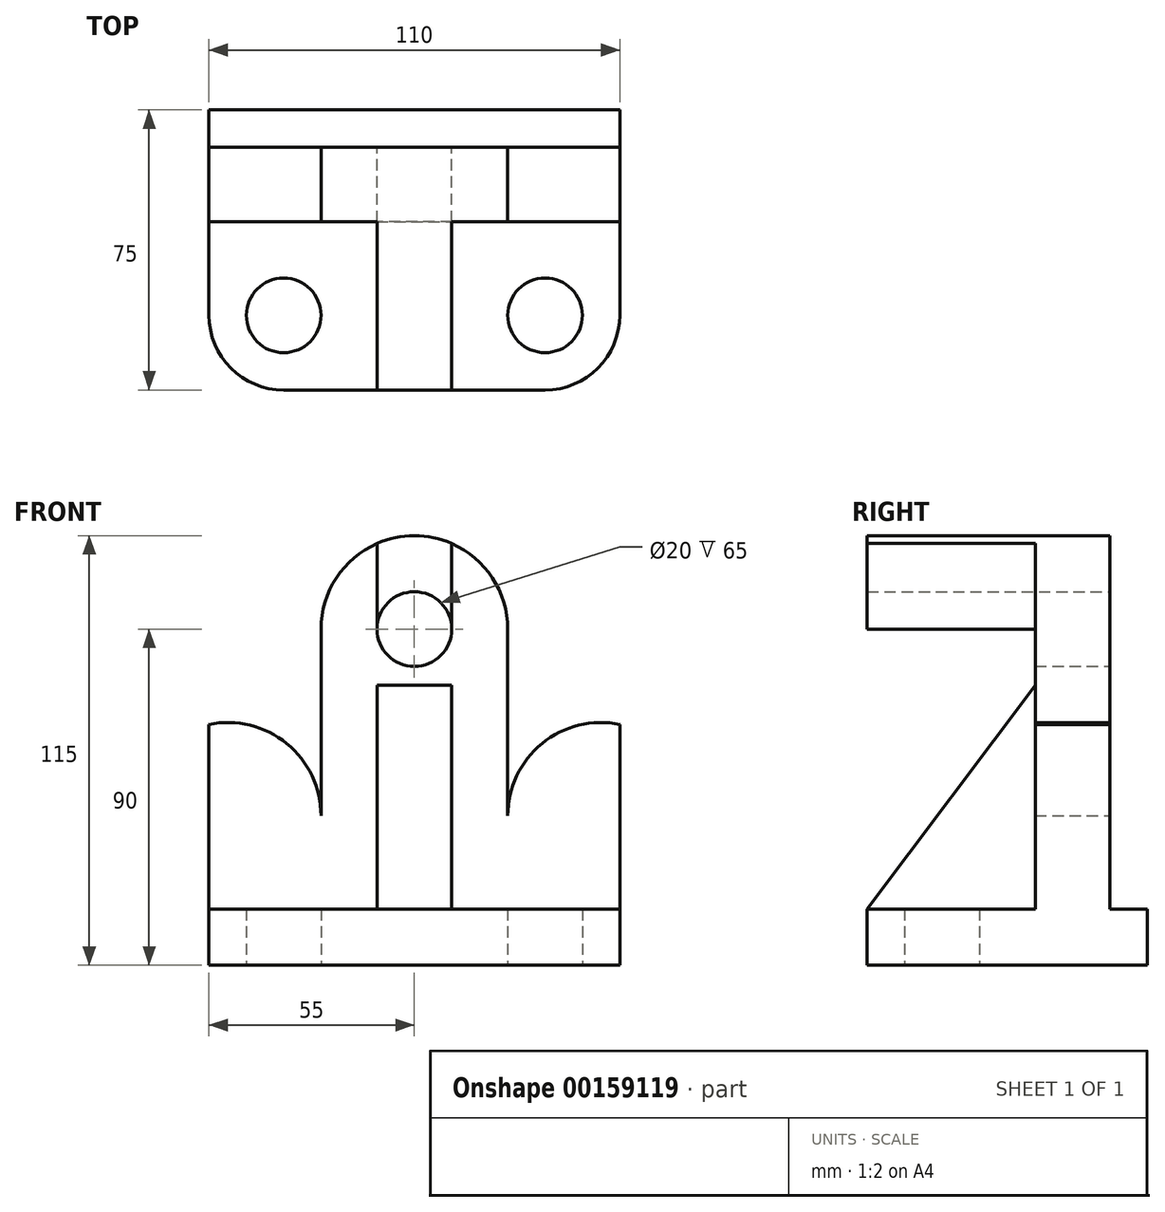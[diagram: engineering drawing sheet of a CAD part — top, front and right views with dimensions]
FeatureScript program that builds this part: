
annotation { "Feature Type Name" : "Feature", "Feature Type Description" : "" }
export const myFeature = defineFeature(function(context is Context, id is Id, definition is map)
    precondition{}
    {
        {
            var Q0;
            Q0=qCreatedBy(makeId("Top.planeOp"),FACE);
            var sketch = newSketch(context, id + "F0", { "sketchPlane" : qUnion([Q0])});
            skLineSegment(sketch, "E0.bottom", {"start": v(0, 0) * mm, "end": v(110, 0) * mm});
            skLineSegment(sketch, "E0.top", {"start": v(0, -75) * mm, "end": v(110, -75) * mm});
            skLineSegment(sketch, "E0.left", {"start": v(0, 0) * mm, "end": v(0, -75) * mm});
            skLineSegment(sketch, "E0.right", {"start": v(110, 0) * mm, "end": v(110, -75) * mm});
            skSolve(sketch);
        }
        {
            var Q0;
            Q0 = qSketchRegion(id + "F0", true);
            extrude(context, id + "F1", {"entities" : qUnion([Q0]), "depth" : (23 * 5) * mm});
        }
        {
            var Q0;
            Q0=makeQuery(id+"F1.opExtrude","SWEPT_FACE",FACE,{"disambiguationData":[OSD([sQuery(id+"F0.wireOp",EDGE,"E0.right")])]});
            var sketch = newSketch(context, id + "F2", { "sketchPlane" : qUnion([Q0])});
            skLineSegment(sketch, "E1.bottom", {"start": v(0, 115) * mm, "end": v(-10, 115) * mm});
            skLineSegment(sketch, "E1.top", {"start": v(0, 15) * mm, "end": v(-10, 15) * mm});
            skLineSegment(sketch, "E1.left", {"start": v(0, 115) * mm, "end": v(0, 15) * mm});
            skLineSegment(sketch, "E1.right", {"start": v(-10, 115) * mm, "end": v(-10, 15) * mm});
            skSolve(sketch);
        }
        {
            var Q0;
            Q0 = qSketchRegion(id + "F2", true);
            extrude(context, id + "F3", {"entities" : qUnion([Q0]), "operationType" : NewBodyOperationType.REMOVE, "endBound" : BoundingType.THROUGH_ALL, "oppositeDirection" : true, "depth" : 25 * mm});
        }
        {
            var Q0;
            Q0=makeQuery(id+"F3.boolean.opBoolean","COPY",FACE,{"derivedFrom":makeQuery(id+"F3.opExtrude","SWEPT_FACE",FACE,{"disambiguationData":[OSD([sQuery(id+"F2.wireOp",EDGE,"E1.right")])]})});
            var sketch = newSketch(context, id + "F4", { "sketchPlane" : qUnion([Q0])});
            skLineSegment(sketch, "E2.bottom", {"start": v(-80, 15) * mm, "end": v(-30, 15) * mm});
            skLineSegment(sketch, "E2.top", {"start": v(-80, 115) * mm, "end": v(-30, 115) * mm});
            skLineSegment(sketch, "E2.left", {"start": v(-80, 15) * mm, "end": v(-80, 115) * mm});
            skLineSegment(sketch, "E2.right", {"start": v(-30, 15) * mm, "end": v(-30, 115) * mm});
            skCircle(sketch, "E3", {"center": v(-5, 40) * mm, "radius": 25 * mm});
            skCircle(sketch, "E4", {"center": v(-105, 40) * mm, "radius": 25 * mm});
            skCircle(sketch, "E5", {"center": v(-55, 90) * mm, "radius": 25 * mm});
            skLineSegment(sketch, "E6.bottom", {"start": v(-110, 15) * mm, "end": v(0, 15) * mm});
            skLineSegment(sketch, "E6.top", {"start": v(-110, 115) * mm, "end": v(0, 115) * mm});
            skLineSegment(sketch, "E6.left", {"start": v(-110, 15) * mm, "end": v(-110, 115) * mm});
            skLineSegment(sketch, "E6.right", {"start": v(0, 15) * mm, "end": v(0, 115) * mm});
            skCircle(sketch, "E7", {"center": v(-55, 90) * mm, "radius": 10 * mm});
            skSolve(sketch);
        }
        {
            var Q0;
            {var subQ1=sQuery(id+"F4.wireOp",EDGE,"E4");var subQ3=sQuery(id+"F4.wireOp",EDGE,"E2.left");var subQ4=makeQuery(id+"F4.imprint","INTERSECT",VERTEX,{"derivedFrom":[subQ3,subQ1]});Q0=makeQuery(id+"F4.imprint","IMPRINT",FACE,{"disambiguationData":[TD([[makeQuery(id+"F4.imprint","IMPRINT",EDGE,{"disambiguationData":[TD([[subQ4,-1.0]])],"derivedFrom":subQ3}),1.0]])]});}
            var Q1;
            {var subQ0=sQuery(id+"F4.wireOp",EDGE,"E6.left");var subQ1=sQuery(id+"F4.wireOp",EDGE,"E4");var subQ2=makeQuery(id+"F4.imprint","INTERSECT",VERTEX,{"disambiguationData":[OD(0.0)],"derivedFrom":[subQ1,subQ0]});Q1=makeQuery(id+"F4.imprint","IMPRINT",FACE,{"disambiguationData":[TD([[makeQuery(id+"F4.imprint","IMPRINT",EDGE,{"disambiguationData":[TD([[subQ2,1.0]])],"derivedFrom":subQ1}),1.0]])]});}
            var Q2;
            {var subQ0=sQuery(id+"F4.wireOp",EDGE,"E6.right");var subQ1=sQuery(id+"F4.wireOp",EDGE,"E3");var subQ2=makeQuery(id+"F4.imprint","INTERSECT",VERTEX,{"disambiguationData":[OD(0.0)],"derivedFrom":[subQ1,subQ0]});Q2=makeQuery(id+"F4.imprint","IMPRINT",FACE,{"disambiguationData":[TD([[makeQuery(id+"F4.imprint","IMPRINT",EDGE,{"disambiguationData":[TD([[subQ2,-1.0]])],"derivedFrom":subQ1}),1.0]])]});}
            var Q3;
            {var subQ3=sQuery(id+"F4.wireOp",EDGE,"E2.right");var subQ6=sQuery(id+"F4.wireOp",EDGE,"E3");var subQ8=makeQuery(id+"F4.imprint","INTERSECT",VERTEX,{"derivedFrom":[subQ3,subQ6]});Q3=makeQuery(id+"F4.imprint","IMPRINT",FACE,{"disambiguationData":[TD([[makeQuery(id+"F4.imprint","IMPRINT",EDGE,{"disambiguationData":[TD([[subQ8,-1.0]])],"derivedFrom":subQ3}),-1.0]])]});}
            var Q4;
            {var subQ0=sQuery(id+"F4.wireOp",EDGE,"E6.top");var subQ1=sQuery(id+"F4.wireOp",EDGE,"E2.right");var subQ2=makeQuery(id+"F4.imprint","INTERSECT",VERTEX,{"derivedFrom":[subQ1,subQ0]});Q4=makeQuery(id+"F4.imprint","IMPRINT",FACE,{"disambiguationData":[TD([[makeQuery(id+"F4.imprint","IMPRINT",EDGE,{"disambiguationData":[TD([[subQ2,1.0]])],"derivedFrom":subQ1}),1.0]])]});}
            var Q5;
            {var subQ0=sQuery(id+"F4.wireOp",EDGE,"E6.top");var subQ1=sQuery(id+"F4.wireOp",EDGE,"E2.left");var subQ2=makeQuery(id+"F4.imprint","INTERSECT",VERTEX,{"derivedFrom":[subQ1,subQ0]});Q5=makeQuery(id+"F4.imprint","IMPRINT",FACE,{"disambiguationData":[TD([[makeQuery(id+"F4.imprint","IMPRINT",EDGE,{"disambiguationData":[TD([[subQ2,1.0]])],"derivedFrom":subQ1}),-1.0]])]});}
            var Q6;
            Q6=makeQuery(id+"F4.imprint","IMPRINT",FACE,{"disambiguationData":[TD([[makeQuery(id+"F4.imprint","IMPRINT",EDGE,{"derivedFrom":sQuery(id+"F4.wireOp",EDGE,"E7")}),1.0]])]});
            extrude(context, id + "F5", {"entities" : qUnion([Q0, Q1, Q2, Q3, Q4, Q5, Q6]), "operationType" : NewBodyOperationType.REMOVE, "endBound" : BoundingType.THROUGH_ALL, "oppositeDirection" : true, "depth" : 25 * mm});
        }
        {
            var Q0;
            Q0=makeQuery(id+"F1.opExtrude","CAP_FACE",FACE,{"disambiguationData":[OSD([sQuery(id+"F0.wireOp",EDGE,"E0.bottom"),sQuery(id+"F0.wireOp",EDGE,"E0.top"),sQuery(id+"F0.wireOp",EDGE,"E0.left"),sQuery(id+"F0.wireOp",EDGE,"E0.right")])],"isStart":true});
            var sketch = newSketch(context, id + "F6", { "sketchPlane" : qUnion([Q0])});
            skCircle(sketch, "E8", {"center": v(90, 55) * mm, "radius": 10 * mm});
            skCircle(sketch, "E9", {"center": v(20, 55) * mm, "radius": 10 * mm});
            skSolve(sketch);
        }
        {
            var Q0;
            Q0 = qSketchRegion(id + "F6", true);
            extrude(context, id + "F7", {"entities" : qUnion([Q0]), "operationType" : NewBodyOperationType.REMOVE, "endBound" : BoundingType.THROUGH_ALL, "oppositeDirection" : true, "depth" : 25 * mm});
        }
        {
            var Q0;
            Q0=makeQuery(id+"F1.opExtrude","SWEPT_FACE",FACE,{"disambiguationData":[OSD([sQuery(id+"F0.wireOp",EDGE,"E0.top")])]});
            var sketch = newSketch(context, id + "F8", { "sketchPlane" : qUnion([Q0])});
            skLineSegment(sketch, "E10.bottom", {"start": v(0, 0) * mm, "end": v(110, 0) * mm});
            skLineSegment(sketch, "E10.top", {"start": v(0, 115) * mm, "end": v(110, 115) * mm});
            skLineSegment(sketch, "E10.left", {"start": v(0, 0) * mm, "end": v(0, 115) * mm});
            skLineSegment(sketch, "E10.right", {"start": v(110, 0) * mm, "end": v(110, 115) * mm});
            skLineSegment(sketch, "E11.bottom", {"start": v(110, 115) * mm, "end": v(65, 115) * mm});
            skLineSegment(sketch, "E11.top", {"start": v(110, 15) * mm, "end": v(65, 15) * mm});
            skLineSegment(sketch, "E11.left", {"start": v(110, 115) * mm, "end": v(110, 15) * mm});
            skLineSegment(sketch, "E11.right", {"start": v(65, 115) * mm, "end": v(65, 15) * mm});
            skLineSegment(sketch, "E12.bottom", {"start": v(0, 115) * mm, "end": v(45, 115) * mm});
            skLineSegment(sketch, "E12.top", {"start": v(0, 15) * mm, "end": v(45, 15) * mm});
            skLineSegment(sketch, "E12.left", {"start": v(0, 115) * mm, "end": v(0, 15) * mm});
            skLineSegment(sketch, "E12.right", {"start": v(45, 115) * mm, "end": v(45, 15) * mm});
            skLineSegment(sketch, "E13.bottom", {"start": v(45, 115) * mm, "end": v(65, 115) * mm});
            skLineSegment(sketch, "E13.top", {"start": v(45, 75) * mm, "end": v(65, 75) * mm});
            skLineSegment(sketch, "E13.left", {"start": v(45, 115) * mm, "end": v(45, 75) * mm});
            skLineSegment(sketch, "E13.right", {"start": v(65, 115) * mm, "end": v(65, 75) * mm});
            skSolve(sketch);
        }
        {
            var Q0;
            {var subQ4=sQuery(id+"F8.wireOp",EDGE,"E12.bottom");Q0=makeQuery(id+"F8.imprint","IMPRINT",FACE,{"disambiguationData":[TD([[makeQuery(id+"F8.imprint","IMPRINT",EDGE,{"derivedFrom":subQ4}),-1.0]])]});}
            var Q1;
            {var subQ2=makeQuery(id+"F1.opExtrude","SWEPT_FACE",FACE,{"disambiguationData":[OSD([sQuery(id+"F0.wireOp",EDGE,"E0.top")])]});var subQ5=sQuery(id+"F8.wireOp",EDGE,"E13.left");var subQ9=makeQuery(id+"F5.boolean.opBoolean","INTERSECT",EDGE,{"derivedFrom":[subQ2,makeQuery(id+"F5.opExtrude","SWEPT_FACE",FACE,{"disambiguationData":[OSD([sQuery(id+"F4.wireOp",EDGE,"E7")])]})]});var subQ11=makeQuery(id+"F8.imprint","INTERSECT",VERTEX,{"derivedFrom":[subQ9,subQ5]});Q1=makeQuery(id+"F8.imprint","IMPRINT",FACE,{"disambiguationData":[TD([[makeQuery(id+"F8.imprint","IMPRINT",EDGE,{"disambiguationData":[TD([[subQ11,-1.0]])],"derivedFrom":subQ9}),1.0]])]});}
            var Q2;
            {var subQ6=sQuery(id+"F8.wireOp",EDGE,"E11.bottom");Q2=makeQuery(id+"F8.imprint","IMPRINT",FACE,{"disambiguationData":[TD([[makeQuery(id+"F8.imprint","IMPRINT",EDGE,{"derivedFrom":subQ6}),1.0]])]});}
            var Q3;
            {var subQ9=sQuery(id+"F8.wireOp",EDGE,"E11.right");Q3=makeQuery(id+"F8.imprint","IMPRINT",FACE,{"disambiguationData":[TD([[makeQuery(id+"F8.imprint","IMPRINT",EDGE,{"derivedFrom":subQ9}),1.0]])]});}
            var Q4;
            {var subQ1=sQuery(id+"F8.wireOp",EDGE,"E12.right");Q4=makeQuery(id+"F8.imprint","IMPRINT",FACE,{"disambiguationData":[TD([[makeQuery(id+"F8.imprint","IMPRINT",EDGE,{"derivedFrom":subQ1}),-1.0]])]});}
            var Q5;
            {var subQ0=sQuery(id+"F8.wireOp",EDGE,"E13.top");Q5=makeQuery(id+"F8.imprint","IMPRINT",FACE,{"disambiguationData":[TD([[makeQuery(id+"F8.imprint","IMPRINT",EDGE,{"derivedFrom":subQ0}),1.0]])]});}
            extrude(context, id + "F9", {"entities" : qUnion([Q0, Q1, Q2, Q3, Q4, Q5]), "operationType" : NewBodyOperationType.REMOVE, "oppositeDirection" : true, "depth" : 45 * mm});
        }
        {
            var Q0;
            Q0=makeQuery(id+"F9.boolean.opBoolean","COPY",FACE,{"derivedFrom":makeQuery(id+"F9.opExtrude","SWEPT_FACE",FACE,{"disambiguationData":[OSD([sQuery(id+"F8.wireOp",EDGE,"E11.right")])]})});
            var sketch = newSketch(context, id + "F10", { "sketchPlane" : qUnion([Q0])});
            skLineSegment(sketch, "E14", {"start": v(-75, 15) * mm, "end": v(-75, 75) * mm});
            skLineSegment(sketch, "E15", {"start": v(-75, 75) * mm, "end": v(-30, 75) * mm});
            skLineSegment(sketch, "E16", {"start": v(-30, 75) * mm, "end": v(-75, 15) * mm});
            skSolve(sketch);
        }
        {
            var Q0;
            Q0 = qSketchRegion(id + "F10", true);
            extrude(context, id + "F11", {"entities" : qUnion([Q0]), "operationType" : NewBodyOperationType.REMOVE, "endBound" : BoundingType.THROUGH_ALL, "oppositeDirection" : true, "depth" : 25 * mm});
        }
        {
            var Q0;
            Q0=makeQuery(id+"F1.opExtrude","SWEPT_EDGE",EDGE,{"disambiguationData":[OSD([sQuery(id+"F0.wireOp",EDGE,"E0.top"),sQuery(id+"F0.wireOp",EDGE,"E0.right")])]});
            var Q1;
            Q1=makeQuery(id+"F1.opExtrude","SWEPT_EDGE",EDGE,{"disambiguationData":[OSD([sQuery(id+"F0.wireOp",EDGE,"E0.top"),sQuery(id+"F0.wireOp",EDGE,"E0.left")])]});
            fillet(context, id + "F12", {"entities" : qUnion([Q0, Q1]), "radius" : 20 * mm, "tangentPropagation" : true, "allowEdgeOverflow" : false});
        }
        {
            var Q0;
            Q0=makeQuery(id+"F1.opExtrude","SWEPT_FACE",FACE,{"disambiguationData":[OSD([sQuery(id+"F0.wireOp",EDGE,"E0.right")])]});
            var sketch = newSketch(context, id + "F13", { "sketchPlane" : qUnion([Q0])});
            skSolve(sketch);
        }
        {
            var Q0;
            Q0 = qSketchRegion(id + "F13", true);
            var Q1;
            Q1=makeQuery(id+"F9.boolean.opBoolean","COPY",FACE,{"derivedFrom":makeQuery(id+"F9.opExtrude","SWEPT_FACE",FACE,{"disambiguationData":[OSD([sQuery(id+"F8.wireOp",EDGE,"E11.right")])]})});
            extrude(context, id + "F14", {"entities" : qUnion([Q0, Q1]), "operationType" : NewBodyOperationType.REMOVE, "endBound" : BoundingType.THROUGH_ALL, "depth" : 25 * mm});
        }
        {
            var Q0;
            Q0=makeQuery(id+"F9.boolean.opBoolean","COPY",FACE,{"derivedFrom":makeQuery(id+"F9.opExtrude","SWEPT_FACE",FACE,{"disambiguationData":[OSD([sQuery(id+"F8.wireOp",EDGE,"E12.right")])]})});
            var sketch = newSketch(context, id + "F15", { "sketchPlane" : qUnion([Q0])});
            skLineSegment(sketch, "E17", {"start": v(30, 15) * mm, "end": v(30, 75) * mm});
            skLineSegment(sketch, "E18", {"start": v(30, 75) * mm, "end": v(75, 15) * mm});
            skLineSegment(sketch, "E19", {"start": v(30, 15) * mm, "end": v(75, 15) * mm});
            skSolve(sketch);
        }
        {
            var Q0;
            Q0 = qSketchRegion(id + "F15", true);
            extrude(context, id + "F16", {"entities" : qUnion([Q0]), "operationType" : NewBodyOperationType.REMOVE, "endBound" : BoundingType.THROUGH_ALL, "depth" : 25 * mm});
        }
    });
